# Revit family: Sofiero-Park-Bench-CC
name_source: partatom
category: Furniture
units: mm (PartAtom-declared; Revit-internal decimal feet)

## family parameters
Always vertical = Yes
Cut with Voids When Loaded = No
OmniClass Number = 23.21.23.13.15
Room Calculation Point = No
Shared = No
Work Plane-Based = No

## types (5) — shared parameters
BIMobject category = Chairs, Stools & Benches
Description = Bench_Sofiero_Cast
Edition number = 1
IFC Classification = Furniture
Manufacturer = Hags
Manufacturer name = HAGS
Masterformat 2014 Code = 12 50 00
Masterformat 2014 Description = Furniture
OmniClass Code = 23-21 25 19 11 13
OmniClass Description = Benches
Product Guid = d9502191-51c7-44ae-a3ea-e9b60ea8e0ac
Product SKU = Bench_Sofiero_Cast
Product data url = https://bimobject.com
Product name = Sofiero Bench
QR code = https://bimobject.com
URL = https://www.hags.com
Uniclass 1.4 Code = JN
Uniclass 1.4 Description = Furniture/Equipment
zero-valued in all types: Default Elevation

## per-type parameters (varying)
| type | Body material | Body material_90 | Construction material | Model | Product url |
| 8037021 Bark Brown / Black | Hags - Wood - Bark brown | Hags - Wood - Bark brown 90 | Hags - Steel - Powder coated - Black | 8037021 | https://hags.se |
| 8037022 Tan / Galvanized | Hags - Wood - Tan | Hags - Wood - Tan 90 | Hags - Steel - Galvanized | 8037022 | https://hags.se |
| 8037024 Green / Black | Hags - Steel - Powder coated - Green | Hags - Steel - Powder coated - Green | Hags - Steel - Powder coated - Black | 8037024 | https://hags.se |
| 8058466 Hardwood / Galvanized | Hags - Hard Wood | Hags - Hard Wood | Hags - Steel - Galvanized | 8058466 | https://www.hags.com |
| 8058450 Hardwood / Black | Hags - Hard Wood | Hags - Hard Wood | Hags - Steel - Powder coated - Black | 8058450 | https://www.hags.com |

## geometry (parser evidence)
native form markers: Sweep x4
no freeform markers — native parametric forms only
